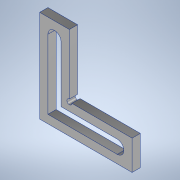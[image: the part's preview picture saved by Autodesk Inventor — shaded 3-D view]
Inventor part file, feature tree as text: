
AUTODESK INVENTOR PART (.ipt)
format: ipt  version: 2022 (Build 260153000, 153)  size: 156,672 bytes
history: native  units: mm
features: extrude x4, sketch x4
ambient origin geometry x8: Origin, YZ Plane, XZ Plane, XY Plane, X Axis, Y Axis, Z Axis, Center Point
bodies: Solid1 (feature_tree)
feature tree (8):
  extrude  "Extrusion1"  Depth=12.0mm
  extrude  "Extrusion2"  Depth=38.0mm
  extrude  "Extrusion3"  Depth=8.0mm
  extrude  "Extrusion4"  Depth=4.0mm
  sketch  "Sketch1"  dims[d0=50.0mm d1=12.0mm]
  sketch  "Sketch2"  dims[d2=38.0mm d3=38.0mm]
  sketch  "Sketch3"  dims[d4=5.0mm d5=0.0mm d6=8.0mm]
  sketch  "Sketch4"  dims[d7=2.0mm d9=4.0mm d10=6.0mm d11=2.0mm d12=8.0mm d13=6.0mm d14=2.0mm d15=4.0mm d16=4.0mm d17=0.0mm d18=3.0mm d19=3.0mm d20=3.0mm d21=3.0mm d24=3.0mm d25=3.0mm d26=5.0mm d27=0.0mm d28=3.0mm d29=5.0mm d30=0.0mm]
